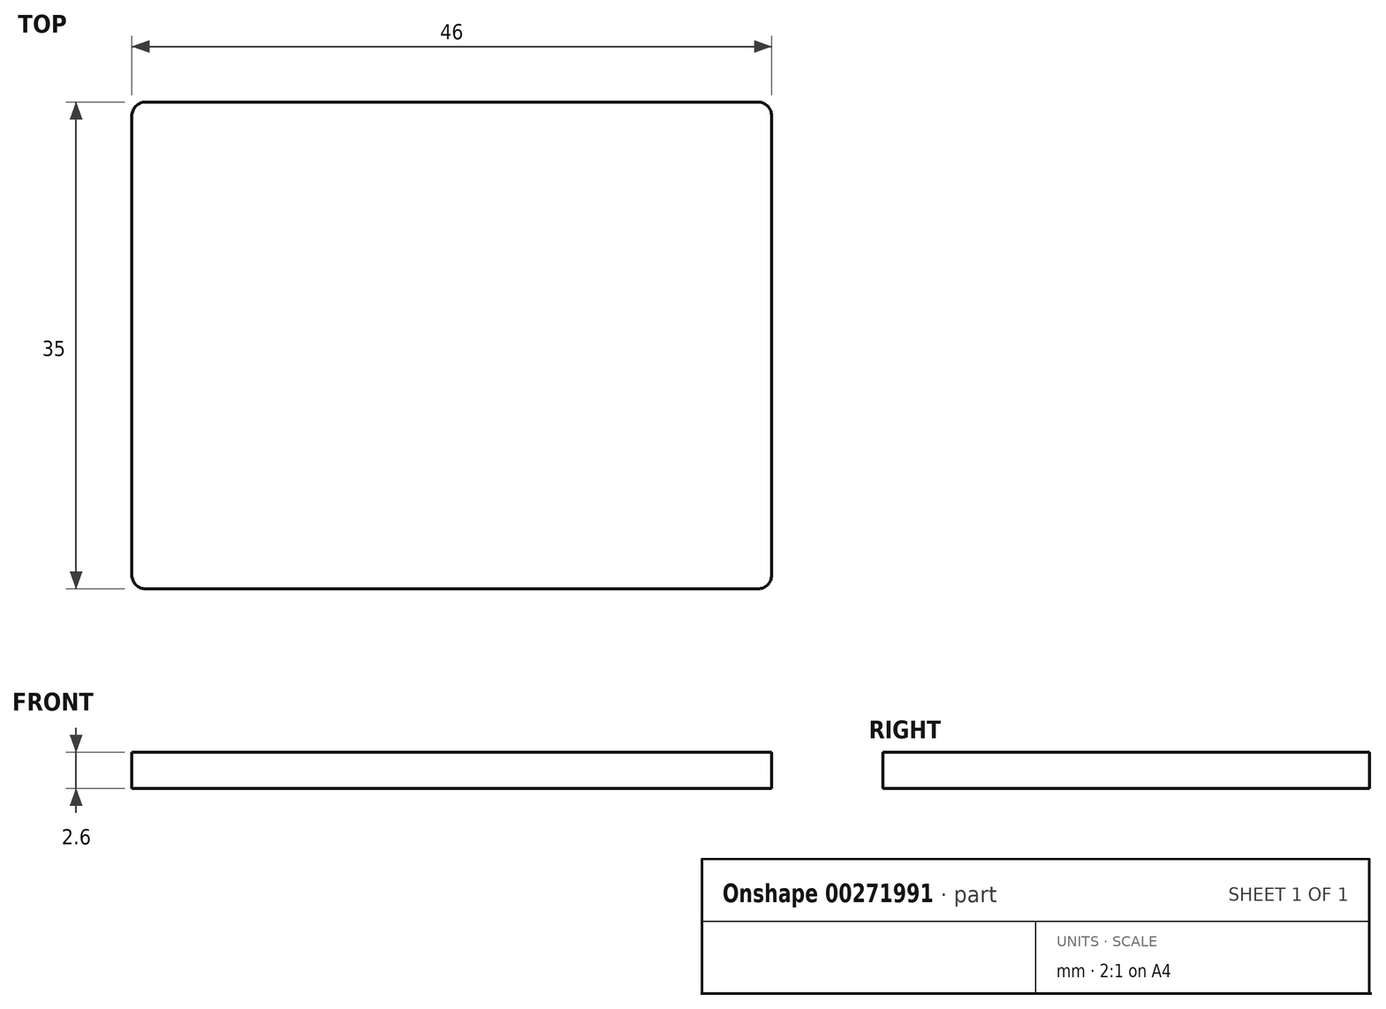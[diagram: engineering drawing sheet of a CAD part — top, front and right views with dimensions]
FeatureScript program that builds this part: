
annotation { "Feature Type Name" : "Feature", "Feature Type Description" : "" }
export const myFeature = defineFeature(function(context is Context, id is Id, definition is map)
    precondition{}
    {
        {
            var Q0;
            Q0=qCreatedBy(makeId("Top.planeOp"),FACE);
            var sketch = newSketch(context, id + "F0", { "sketchPlane" : qUnion([Q0])});
            skLineSegment(sketch, "E0.bottom", {"start": v(23, -17.5) * mm, "end": v(-23, -17.5) * mm});
            skLineSegment(sketch, "E0.top", {"start": v(23, 17.5) * mm, "end": v(-23, 17.5) * mm});
            skLineSegment(sketch, "E0.left", {"start": v(23, -17.5) * mm, "end": v(23, 17.5) * mm});
            skLineSegment(sketch, "E0.right", {"start": v(-23, -17.5) * mm, "end": v(-23, 17.5) * mm});
            skPoint(sketch, "E0.middle", {"position": v(0, 0) * mm});
            skSolve(sketch);
        }
        {
            var Q0;
            Q0 = qSketchRegion(id + "F0", true);
            extrude(context, id + "F1", {"entities" : qUnion([Q0]), "depth" : 2.6 * mm});
        }
        {
            var Q0;
            Q0=makeQuery(id+"F1.opExtrude","SWEPT_EDGE",EDGE,{"disambiguationData":[OSD([sQuery(id+"F0.wireOp",EDGE,"E0.bottom"),sQuery(id+"F0.wireOp",EDGE,"E0.left")])]});
            var Q1;
            Q1=makeQuery(id+"F1.opExtrude","SWEPT_EDGE",EDGE,{"disambiguationData":[OSD([sQuery(id+"F0.wireOp",EDGE,"E0.bottom"),sQuery(id+"F0.wireOp",EDGE,"E0.right")])]});
            var Q2;
            Q2=makeQuery(id+"F1.opExtrude","SWEPT_EDGE",EDGE,{"disambiguationData":[OSD([sQuery(id+"F0.wireOp",EDGE,"E0.top"),sQuery(id+"F0.wireOp",EDGE,"E0.right")])]});
            var Q3;
            Q3=makeQuery(id+"F1.opExtrude","SWEPT_EDGE",EDGE,{"disambiguationData":[OSD([sQuery(id+"F0.wireOp",EDGE,"E0.top"),sQuery(id+"F0.wireOp",EDGE,"E0.left")])]});
            fillet(context, id + "F2", {"entities" : qUnion([Q0, Q1, Q2, Q3]), "radius" : 1 * mm, "tangentPropagation" : true, "allowEdgeOverflow" : false});
        }
    });
